# Revit family: PRD_AR_SntryTwlDspslBins_STRATOSSanitaryTowelAndDisposalBin_STR611
name_source: partatom
category: Specialty Equipment
units: mm (PartAtom-declared; Revit-internal decimal feet)

## family parameters
Cut with Voids When Loaded = No
Host = Face
OmniClass Number = 23.40.20.31.11
OmniClass Title = Bins
Part Type = Normal
Room Calculation Point = No
Round Connector Dimension = Use Diameter
Shared = No

## types (1)
- STR611
    AssetType = Fixed
    BIMObjectName = PRD_AR_SanitaryTowelDisposalBins_STRATOSSanitaryTowelAndDisposalBin_STR611
    Category = Pr_40_50_07_76, Sanitary towel disposal bins
    Color = Stainless steel
    Default Elevation = 820 mm  [stored 2.69029 ft]
    Description = STRATOS hygiene waste bin for wall mounting, stainless steel, surface satin finished, material thickness 1.5 mm, curved front, approx. 3.8 litre capacity, hinged self-closing front, integrated plastic container for waste removal, including mounting material.
    DurationUnit = year
    Features = stainless steel, surface satin finished, wall mounting
    FillingQuantity = 3.80 L
    Finish = Satin finished
    FinishAndColour = Stainless steel, satin finished
    Form = Wall mounted
    GrossWeight = 3.72 kg
    IfcExportAs = IfcFurnitureType
    IfcExportType = NOTDEFINED
    IntegralAccessories = includes mounting materials
    MainColor = Stainless steel
    Manufacturer = KWC Group Management AG
    ManufacturerName = KWC Group Management AG
    ManufacturerURL = www.kwc-professional.com
    Material = Stainless steel
    Materials = Stainless steel 1.4301
    Model = STR611
    ModelNumber = 3600008914
    ModelReference = STR611
    NBSDescription = Sanitary towel disposal bins
    NBSReference = 45-35-72/350
    Name = STRATOS Sanitary towel and disposal bin STR611
    NetWeight = 3.42 kg
    NominalDepth = 134 mm
    NominalHeight = 305 mm  [stored 1.00066 ft]
    NominalLength = 205 mm  [stored 0.672572 ft]
    NominalWidth = 205 mm  [stored 0.672572 ft]
    ProductInformation = http://pim.kwc.com
    Size = 205x305x134 mm
    Style = Sanitary towel and disposal bin
    URL = www.kwc-professional.com
    Uniclass2015Code = Pr_40_50_07_76
    Uniclass2015Title = Sanitary towel disposal bins
    Uniclass2015Version = Products v1.7
    Version = 1
    WarrantyDurationUnit = year
    WasteBinMaterial = PRD_AR_StainlessSteel_SatinFinished

note: [stored X ft] marks values corroborated as IEEE doubles in the binary element streams (Revit-internal decimal feet)

## geometry (parser evidence)
native form markers: Sweep x2
no freeform markers — native parametric forms only
